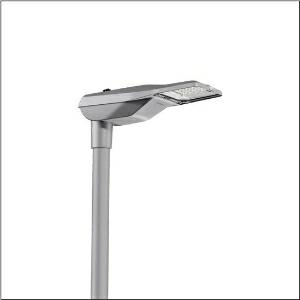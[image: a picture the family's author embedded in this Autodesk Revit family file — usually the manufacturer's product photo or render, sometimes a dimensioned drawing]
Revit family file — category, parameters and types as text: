
# Revit family: streetlight_sl_21_iq_micro___p0_8ab_5xe1r31v08cb_c843
name_source: partatom
category: Lighting Fixtures
units: mm (PartAtom-declared; Revit-internal decimal feet)

## family parameters
Cut with Voids When Loaded = No
Host = Face
Light Source = No
Part Type = Normal
Room Calculation Point = No
Round Connector Dimension = Use Diameter
Shared = No

## types (1)
- --- (1 x LED, 2570 lm, 19.1 W, 3000K)
    Apparent Load = 19 VA
    CIE Flux Codes = 36 71 98 100 100
    Color Rendering = 70
    Color Temperature = 3000K
    Default Elevation = 1800 mm
    Description = Streetlight SL 21 iQ micro, mast luminaire, primary light control with lens, of PMMA, primary optical cover: cover, of toughened safety glass, transparent, light distribution: P0.8aB, light emission: direct distribution, primary light characteristic: asymmetric, installation type: post-top, side-entry, LED, High Power LED, rated luminous flux: 2.570lm, luminous efficacy: 135lm/W, light colour: 730, colour temperature: 3000K, control gear: iQ-Street Remote, D4i with power reduction, control: pre-setting: logarithmic dimming characteristic, Street-Remote, Auto-Match, Temp-Guard, Lumen-Switch, Night-Set, Smart-Wire, Light-Fading, Desk-Remote (wireless, voltage-free reading and setting of iQ features in the workshop via application-optimized NFC function/RFID function), optimised constant luminous flux control (CLO 2.0), mains connection: 220..240V, AC, 50/60Hz, start of lifetime: 19W, end of service life: 20W, reduction: 9W, luminaire housing, of diecast aluminium, powder-coated, SITECO metallic grey (DB 702S), corrosivity category C5 high according to DIN EN ISO 12944, please order mast flange separately, inclination adjustable: 0°, 5°, 10°, 15°, sealing non-destructively replaceable, multi-level sealing system, length: 528mm, width: 235mm, height: 110mm, mast flange for spigot size: 42mm (side-entry): 5XC10008XM4, 60/48mm (side-entry/post-top): 5XC10108XM2, 76/60mm (side-entry/post-top): 5XC10108XM1, mounting height: 4..8m, Smart Interface above, protection rating (complete): IP66, insulation class (complete): insulation class II (safety insulation), certification: CE, ENEC, ENEC+, VDE, impact resistance: IK10, permissible operating ambient temperature for outdoor applications: -40..+50°C, standard-compliant lighting for roads and squares, packaging unit: 1 piece

Light Distribution: P0.8aB
    Height = 110 mm
    Lamp = 1 x LED
    Lamp Light Flux = 2570 lm
    Lamp Power = 19.1 W
    Lamp count = 1
    Length = 528 mm
    Luminous efficacy = 135 lm/W
    Manufacturer = Siteco
    ModVariant = No
    Model = 5XE1R31V08CB
    Number of Poles = 1
    OnlyDefault = Yes
    Power Factor = 1
    Product Name = Streetlight SL 21 iQ micro | P0.8aB
    Product group = mast luminaire | pylon top
    ProductGroupID = 6100
    Protection Class = Protection class II
    Protection Degree = IP 66
    RLX_Detail_Level = 1
    RLX_Emergency_Light_Flux = 0 lm
    RLX_Emergency_Type = 0
    RLX_Emergency_Type_DB = No
    RlxData = <blob elided: 98121 chars, md5=0ef3e2d0>
    Socket = socket
    Standby Power = 0 W
    System Light Flux = 2570 lm
    System Power = 19 W
    Type Comments = factory setting: luminous flux: 100 % | dim-lin: 254 | 387 mA
    Type Image = l_1277292.jpg
    URL = http://relux.com
    VarID = @adj_083399
    Voltage = 0 V
    Weight = 0.00 kg
    Width = 235 mm

## geometry (parser evidence)
native form markers: Blend x4, Sweep x11
no freeform markers — native parametric forms only
